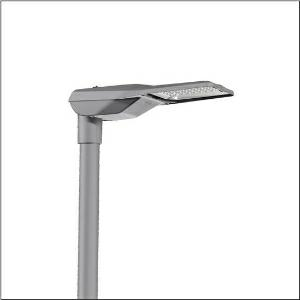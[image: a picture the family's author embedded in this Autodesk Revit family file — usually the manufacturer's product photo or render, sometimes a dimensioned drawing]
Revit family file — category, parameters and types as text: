
# Revit family: streetlight_sl_21_mini___st1_0a_5xe2d43s08hb_695f
name_source: partatom
category: Lighting Fixtures
units: mm (PartAtom-declared; Revit-internal decimal feet)

## family parameters
Cut with Voids When Loaded = No
Host = Face
Light Source = No
Part Type = Normal
Room Calculation Point = No
Round Connector Dimension = Use Diameter
Shared = No

## types (1)
- --- (1 x LED, 9430 lm, 66 W, 4000K)
    Apparent Load = 66 VA
    CIE Flux Codes = 37 72 97 100 100
    Color Rendering = 70
    Color Temperature = 4000K
    Default Elevation = 1800 mm
    Description = Streetlight SL 21 mini, mast luminaire, primary light control with lens, of PMMA, primary optical cover: cover, of toughened safety glass, transparent, light distribution: ST1.0a, light emission: direct distribution, primary light characteristic: asymmetric, installation type: side-entry, post-top, LED, High Power LED, rated luminous flux: 9.430lm, luminous efficacy: 143lm/W, light colour: 740, colour temperature: 4000K, control gear: D4i, control: overheat protection, constant luminous flux control, time-dependent luminous flux control, flexible luminous flux parameterisation, pre-setting: logarithmic dimming characteristic, mains connection: 220..240V, AC, 50/60Hz, start of lifetime: 66W, end of service life: 69W, reduction: 30W, luminaire housing, of diecast aluminium, powder-coated, Siteco® metallic grey (DB 702S), corrosivity category C5 mid according to DIN EN ISO 12944, please order mast flange separately, inclination adjustable: 0°, 5°, 10°, 15°, sealing non-destructively replaceable, multi-level sealing system, length: 628mm, width: 235mm, height: 110mm, mast flange for spigot size: 42mm (side-entry): 5XC10008XM4, 60/48mm (side-entry/post-top): 5XC10108XM2, 76/60mm (side-entry/post-top): 5XC10108XM1, mounting height: 4..8m, Smart Interface above, protection rating (complete): IP66, insulation class (complete): insulation class II (safety insulation), certification: CE, ENEC, ENEC+, VDE, impact resistance: IK10, permissible operating ambient temperature for outdoor applications: -40..+50°C, standard-compliant lighting for roads and squares, packaging unit: 1 piece

Light Distribution: ST1.0a
    Height = 110 mm
    Lamp = 1 x LED
    Lamp Light Flux = 9430 lm
    Lamp Power = 66 W
    Lamp count = 1
    Length = 625 mm
    Luminous efficacy = 143 lm/W
    Manufacturer = Siteco
    ModVariant = No
    Model = 5XE2D43S08HB
    Number of Poles = 1
    OnlyDefault = Yes
    Power Factor = 1
    Product Name = Streetlight SL 21 mini | ST1.0a
    Product group = mast luminaire | pylon top
    ProductGroupID = 6100
    Protection Class = Protection class II
    Protection Degree = IP 66
    RLX_Detail_Level = 1
    RLX_Emergency_Light_Flux = 0 lm
    RLX_Emergency_Type = 0
    RLX_Emergency_Type_DB = No
    RlxData = <blob elided: 26141 chars, md5=e9158907>
    Socket = socket
    Standby Power = 0 W
    System Light Flux = 9430 lm
    System Power = 66 W
    Type Comments = factory setting: luminous flux: 100 % | dim-lin: 254 | 670 mA
    Type Image = l_1003515.jpg
    URL = http://relux.com
    VarID = @adj_188618
    Voltage = 0 V
    Weight = 0.00 kg
    Width = 234 mm

## geometry (parser evidence)
native form markers: Blend x4, Sweep x12
no freeform markers — native parametric forms only
